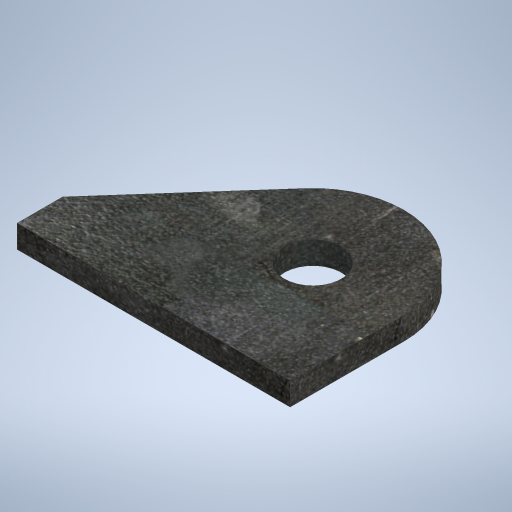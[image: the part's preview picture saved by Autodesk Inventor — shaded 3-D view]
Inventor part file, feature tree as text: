
AUTODESK INVENTOR PART (.ipt)
format: ipt  version: 2023 (Build 270158000, 158)  size: 1,925,632 bytes
history: native  units: mm
features: other x3, sketch x1
ambient origin geometry x8: Origin, YZ Plane, XZ Plane, XY Plane, X Axis, Y Axis, Z Axis, Center Point
bodies: Body1 (feature_tree)
feature tree (4):
  other  "Cara2"
  sketch  "Boceto2"  dims[d7=50.0mm d8=20.0mm d9=40.0mm d10=120.0mm d11=25.0mm d12=10.0mm]
  other  "Placa2"
  other  "Definición1"
